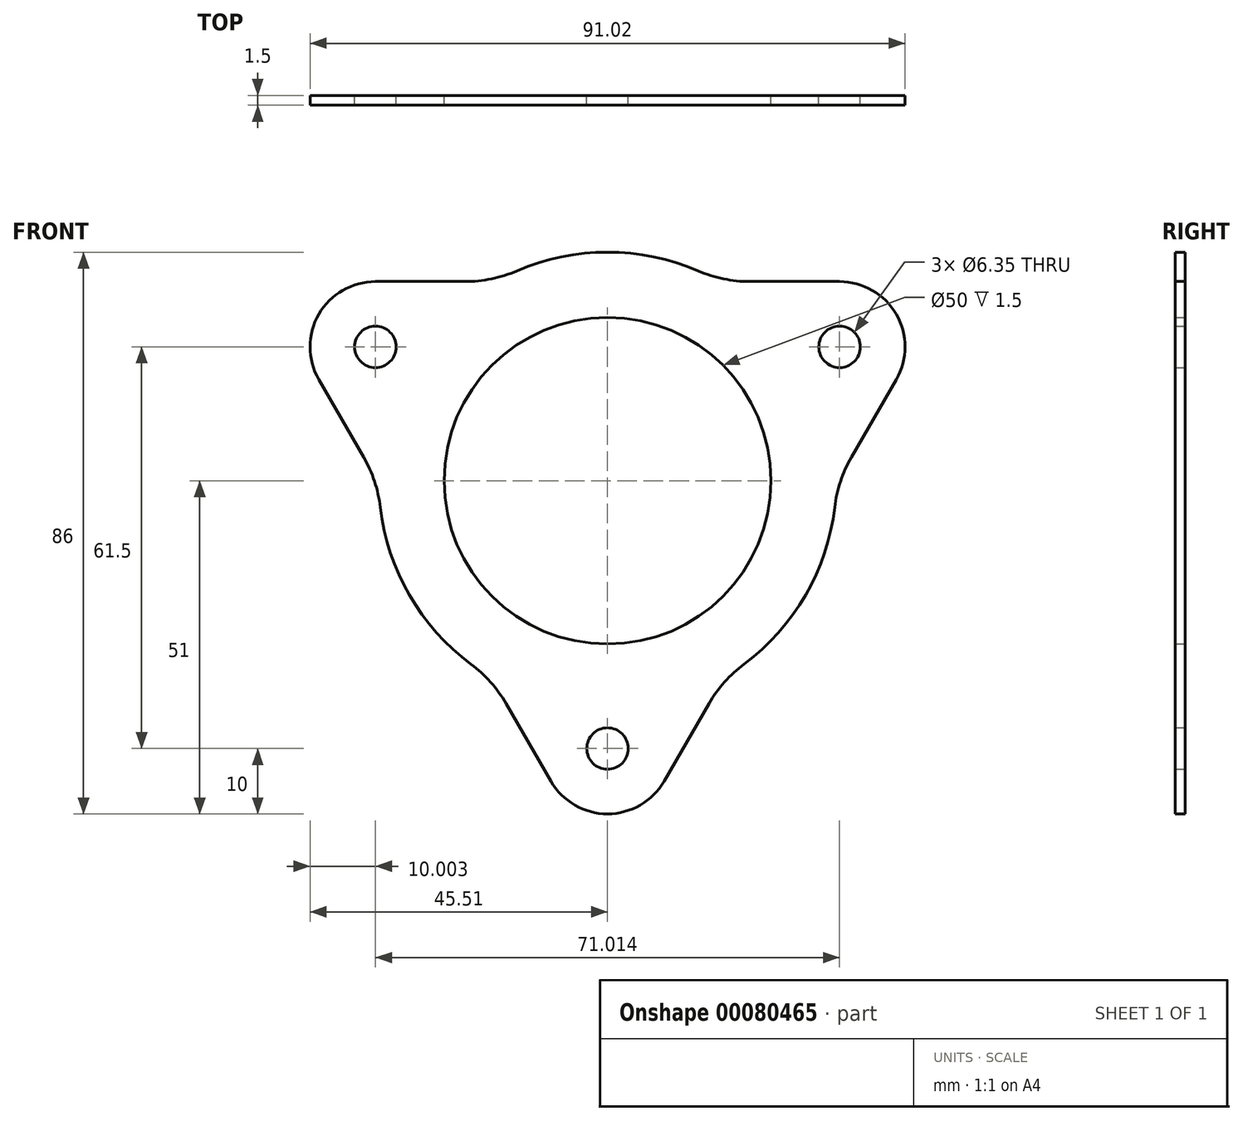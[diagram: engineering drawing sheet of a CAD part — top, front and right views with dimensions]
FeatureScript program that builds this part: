
annotation { "Feature Type Name" : "Feature", "Feature Type Description" : "" }
export const myFeature = defineFeature(function(context is Context, id is Id, definition is map)
    precondition{}
    {
        {
            var Q0;
            Q0=qCreatedBy(makeId("Front.planeOp"),FACE);
            var sketch = newSketch(context, id + "F0", { "sketchPlane" : qUnion([Q0])});
            skCircle(sketch, "E0", {"center": v(0, 0) * mm, "radius": 25 * mm});
            skCircle(sketch, "E1", {"center": v(0, 0) * mm, "radius": 41 * mm, "construction": true});
            skLineSegment(sketch, "E2", {"start": v(0, 0) * mm, "end": v(35.5, 20.5) * mm, "construction": true});
            skLineSegment(sketch, "E3", {"start": v(0, 0) * mm, "end": v(0, -41) * mm, "construction": true});
            skLineSegment(sketch, "E4", {"start": v(0, 0) * mm, "end": v(-35.5, 20.5) * mm, "construction": true});
            skCircle(sketch, "E5", {"center": v(-35.5, 20.5) * mm, "radius": 3.17 * mm});
            skCircle(sketch, "E6", {"center": v(35.5, 20.5) * mm, "radius": 3.17 * mm});
            skCircle(sketch, "E7", {"center": v(0, -41) * mm, "radius": 3.17 * mm});
            skArc(sketch, "E8", {"start": v(-8.66, -46) * mm, "mid": v(0, -51) * mm, "end": v(8.66, -46) * mm});
            skArc(sketch, "E9", {"start": v(-35.5, 30.5) * mm, "mid": v(-44.17, 25.5) * mm, "end": v(-44.17, 15.5) * mm});
            skArc(sketch, "E10", {"start": v(44.17, 15.5) * mm, "mid": v(44.17, 25.5) * mm, "end": v(35.5, 30.5) * mm});
            skLineSegment(sketch, "E11", {"start": v(-35.5, 30.5) * mm, "end": v(-17.17, 30.5) * mm});
            skLineSegment(sketch, "E12", {"start": v(-44.17, 15.5) * mm, "end": v(-35, -0.38) * mm});
            skLineSegment(sketch, "E13", {"start": v(8.66, -46) * mm, "end": v(17.83, -30.12) * mm});
            skArc(sketch, "E14", {"start": v(-35, -0.38) * mm, "mid": v(-30.31, -17.5) * mm, "end": v(-17.83, -30.12) * mm});
            skLineSegment(sketch, "E15.trimOffspring", {"start": v(17.17, 30.5) * mm, "end": v(35.5, 30.5) * mm});
            skLineSegment(sketch, "E16.trimOffspring", {"start": v(-17.83, -30.12) * mm, "end": v(-8.66, -46) * mm});
            skArc(sketch, "E17.trimOffspring", {"start": v(17.83, -30.12) * mm, "mid": v(30.31, -17.5) * mm, "end": v(35, -0.38) * mm});
            skLineSegment(sketch, "E18.trimOffspring", {"start": v(35, -0.38) * mm, "end": v(44.17, 15.5) * mm});
            skArc(sketch, "E19.trimOffspring", {"start": v(17.17, 30.5) * mm, "mid": v(0, 35) * mm, "end": v(-17.17, 30.5) * mm});
            skSolve(sketch);
        }
        {
            var Q0;
            Q0 = qSketchRegion(id + "F0", true);
            extrude(context, id + "F1", {"entities" : qUnion([Q0]), "depth" : 1.5 * mm});
        }
        {
            var Q0;
            Q0=makeQuery(id+"F1.opExtrude","SWEPT_EDGE",EDGE,{"disambiguationData":[OSD([sQuery(id+"F0.wireOp",EDGE,"E17.trimOffspring"),sQuery(id+"F0.wireOp",EDGE,"E18.trimOffspring")])]});
            var Q1;
            Q1=makeQuery(id+"F1.opExtrude","SWEPT_EDGE",EDGE,{"disambiguationData":[OSD([sQuery(id+"F0.wireOp",EDGE,"E15.trimOffspring"),sQuery(id+"F0.wireOp",EDGE,"E19.trimOffspring")])]});
            var Q2;
            Q2=makeQuery(id+"F1.opExtrude","SWEPT_EDGE",EDGE,{"disambiguationData":[OSD([sQuery(id+"F0.wireOp",EDGE,"E11"),sQuery(id+"F0.wireOp",EDGE,"E19.trimOffspring")])]});
            var Q3;
            Q3=makeQuery(id+"F1.opExtrude","SWEPT_EDGE",EDGE,{"disambiguationData":[OSD([sQuery(id+"F0.wireOp",EDGE,"E12"),sQuery(id+"F0.wireOp",EDGE,"E14")])]});
            var Q4;
            Q4=makeQuery(id+"F1.opExtrude","SWEPT_EDGE",EDGE,{"disambiguationData":[OSD([sQuery(id+"F0.wireOp",EDGE,"E14"),sQuery(id+"F0.wireOp",EDGE,"E16.trimOffspring")])]});
            var Q5;
            Q5=makeQuery(id+"F1.opExtrude","SWEPT_EDGE",EDGE,{"disambiguationData":[OSD([sQuery(id+"F0.wireOp",EDGE,"E13"),sQuery(id+"F0.wireOp",EDGE,"E17.trimOffspring")])]});
            fillet(context, id + "F2", {"entities" : qUnion([Q0, Q1, Q2, Q3, Q4, Q5]), "radius" : 20 * mm, "tangentPropagation" : true, "allowEdgeOverflow" : false});
        }
    });
